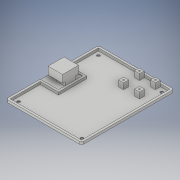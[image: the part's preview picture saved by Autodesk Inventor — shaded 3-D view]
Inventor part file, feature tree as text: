
AUTODESK INVENTOR PART (.ipt)
format: ipt  version: 2019 (Build 230136000, 136)  size: 1,417,728 bytes
history: native  units: mm
features: sketch x13, extrude x12, direct_edit x6, move_body x6, chamfer x2
ambient origin geometry x8: Origin, YZ Plane, XZ Plane, XY Plane, X Axis, Y Axis, Z Axis, Center Point
bodies: Solid1 (feature_tree)
feature tree (39):
  extrude  "Extrusion1"  Depth=110.0mm
  extrude  "Extrusion2"  Depth=5.0mm
  extrude  "Extrusion3"  Depth=21.8mm TaperAngle=0.0deg
  extrude  "Extrusion4"  Depth=13.0mm
  extrude  "Extrusion5"  Depth=19.0mm
  extrude  "Extrusion6"  Depth=9.0mm TaperAngle=0.0deg
  extrude  "Extrusion7"  Depth=3.0mm TaperAngle=0.0deg
  extrude  "Extrusion8"  Depth=5.0mm
  extrude  "Extrusion9"  Depth=5.0mm
  direct_edit  "Direct Edit1"
  extrude  "Extrusion10"  Depth=5.0mm
  extrude  "Extrusion11"  Depth=5.0mm
  direct_edit  "Direct Edit2"
  direct_edit  "Direct Edit3"
  direct_edit  "Direct Edit4"
  direct_edit  "Direct Edit5"
  sketch  "Sketch12"  dims[d31=3.5mm d32=3.5mm]
  direct_edit  "Direct Edit6"
  extrude  "Extrusion12"  Depth=3.5mm
  chamfer  "Chamfer1"  Distance=3.5mm
  chamfer  "Chamfer2"  Distance=5.0mm
  sketch  "Sketch1"  dims[d2=90.0mm d3=110.0mm]
  sketch  "Sketch2"  dims[d4=5.0mm d5=0.0mm d6=28.6mm]
  sketch  "Sketch3"  dims[d7=21.8mm d8=0.5mm d9=0.0mm]
  sketch  "Sketch4"  dims[d10=10.3mm d11=13.0mm]
  sketch  "Sketch5"  dims[d12=4.8mm d13=0.0mm d14=19.0mm]
  sketch  "Sketch6"  dims[d15=17.2mm d16=9.0mm d17=0.0mm]
  sketch  "Sketch7"  dims[d20=2.5mm d21=3.0mm d22=0.0mm]
  sketch  "Sketch8"  dims[d23=5.0mm d24=5.0mm]
  sketch  "Sketch9"  dims[d25=5.0mm d26=5.0mm]
  sketch  "Sketch10"  dims[d27=5.0mm d28=5.0mm]
  sketch  "Sketch11"  dims[d29=5.0mm d30=5.0mm]
  sketch  "Sketch13"  dims[d33=3.5mm d34=3.5mm d35=5.0mm d36=0.0mm d37=10.0mm d38=10.0mm d39=25.0mm d40=25.0mm d41=6.0mm d42=6.0mm d43=6.0mm d44=6.0mm d45=6.0mm d46=6.0mm d47=6.0mm d48=6.0mm d49=7.0mm d50=0.0mm d51=2.0mm d52=2.0mm d53=2.0mm d54=2.0mm d55=3.0mm d56=0.0mm d57=1.0mm d58=1.0mm d59=1.0mm d60=1.0mm d61=3.0mm d62=0.0mm d63=0.0mm d64=0.0mm d65=-0.3mm d66=0.6mm d67=0.0mm d68=6.0mm d69=6.0mm d70=6.0mm d71=6.0mm d72=1.2mm d73=0.0mm d74=-4.0mm d75=0.0mm d76=0.0mm d77=0.0mm d78=0.0mm d79=-1.53mm d80=0.0mm d81=0.0mm d82=1.5mm d83=4.0mm d84=0.0mm d85=0.0mm d88=0.5mm d89=0.0mm d90=0.0mm d91=4.0mm d92=10.0mm d93=4.0mm d94=10.0mm d95=1.5mm d96=0.0mm d97=2.0mm d98=2.0mm d99=45.0deg d100=2.0mm d101=2.0mm d102=45.0deg]
  move_body  "Move1"
  move_body  "Move2"
  move_body  "Move3"
  move_body  "Move4"
  move_body  "Move5"
  move_body  "Move6"
